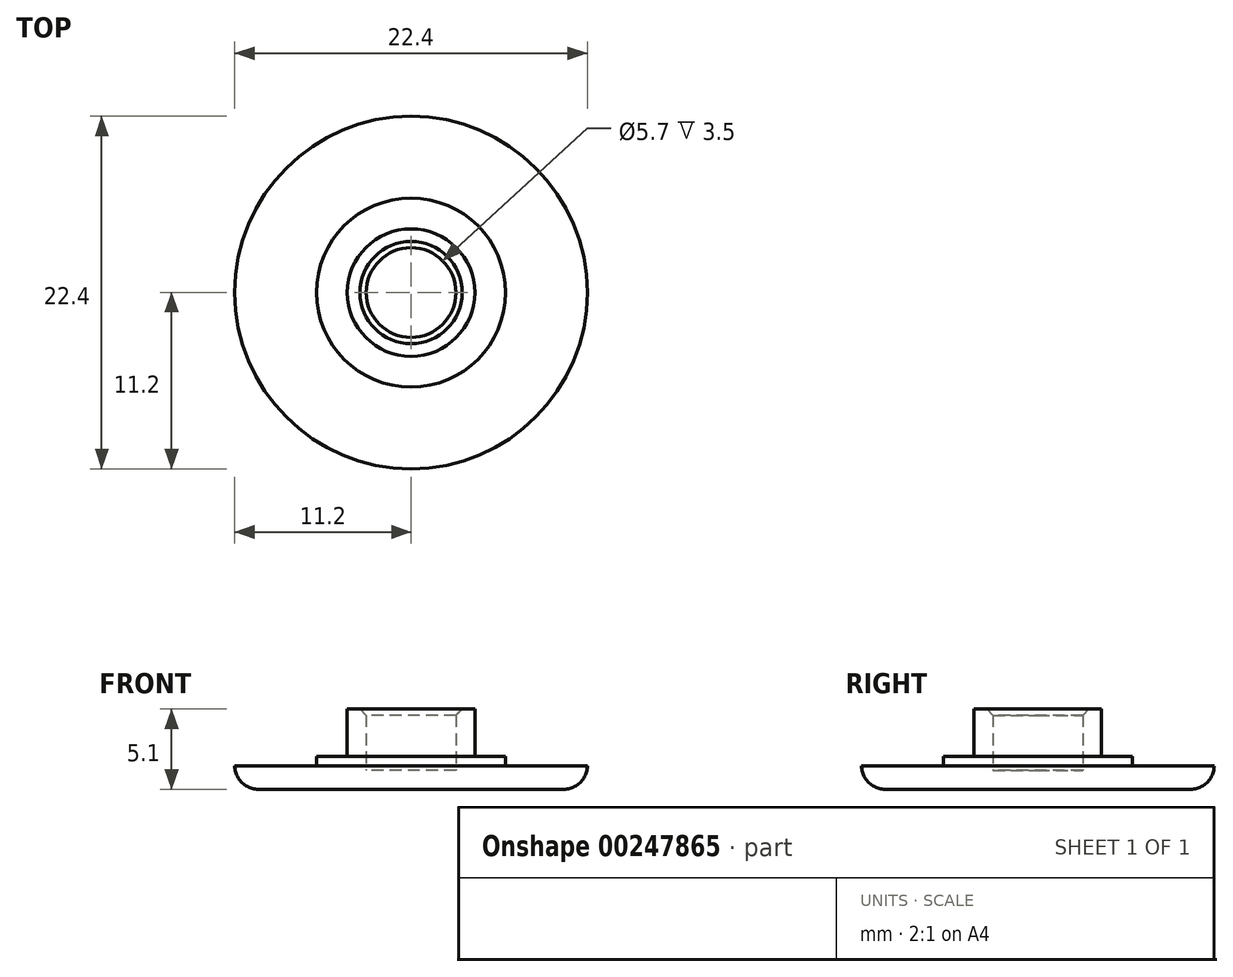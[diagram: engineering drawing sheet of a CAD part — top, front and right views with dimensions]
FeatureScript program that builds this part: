
annotation { "Feature Type Name" : "Feature", "Feature Type Description" : "" }
export const myFeature = defineFeature(function(context is Context, id is Id, definition is map)
    precondition{}
    {
        {
            var Q0;
            Q0=qCreatedBy(makeId("Top.planeOp"),FACE);
            var sketch = newSketch(context, id + "F0", { "sketchPlane" : qUnion([Q0])});
            skCircle(sketch, "E0", {"center": v(0, 0) * mm, "radius": 11.2 * mm});
            skSolve(sketch);
        }
        {
            var Q0;
            Q0=makeQuery(id+"F0.imprint","IMPRINT",FACE,{"disambiguationData":[TD([[makeQuery(id+"F0.imprint","IMPRINT",EDGE,{"derivedFrom":sQuery(id+"F0.wireOp",EDGE,"E0")}),1.0]])]});
            extrude(context, id + "F1", {"entities" : qUnion([Q0]), "oppositeDirection" : true, "depth" : 1.5 * mm, "offsetDistance" : 25 * mm});
        }
        {
            var Q0;
            Q0=makeQuery(id+"F1.opExtrude","CAP_FACE",FACE,{"disambiguationData":[OSD([sQuery(id+"F0.wireOp",EDGE,"E0")])],"isStart":true});
            var sketch = newSketch(context, id + "F2", { "sketchPlane" : qUnion([Q0])});
            skCircle(sketch, "E1", {"center": v(0, 0) * mm, "radius": 6 * mm});
            skSolve(sketch);
        }
        {
            var Q0;
            Q0 = qSketchRegion(id + "F2", true);
            extrude(context, id + "F3", {"entities" : qUnion([Q0]), "operationType" : NewBodyOperationType.ADD, "depth" : 0.6 * mm, "offsetDistance" : 25 * mm});
        }
        {
            var Q0;
            Q0=makeQuery(id+"F3.opExtrude","CAP_FACE",FACE,{"disambiguationData":[OSD([sQuery(id+"F2.wireOp",EDGE,"E1")])],"isStart":false});
            var sketch = newSketch(context, id + "F4", { "sketchPlane" : qUnion([Q0])});
            skCircle(sketch, "E2", {"center": v(0, 0) * mm, "radius": 4.05 * mm});
            skSolve(sketch);
        }
        {
            var Q0;
            Q0 = qSketchRegion(id + "F4", true);
            extrude(context, id + "F5", {"entities" : qUnion([Q0]), "operationType" : NewBodyOperationType.ADD, "depth" : 3 * mm, "offsetDistance" : 25 * mm});
        }
        {
            var Q0;
            Q0=makeQuery(id+"F5.opExtrude","CAP_FACE",FACE,{"disambiguationData":[OSD([sQuery(id+"F4.wireOp",EDGE,"E2")])],"isStart":false});
            shell(context, id + "F6", {"entities" : qUnion([Q0]), "thickness" : 1.2 * mm});
        }
        {
            var Q0;
            Q0=makeQuery(id+"F1.opExtrude","CAP_EDGE",EDGE,{"disambiguationData":[OSD([sQuery(id+"F0.wireOp",EDGE,"E0")])],"isStart":false});
            fillet(context, id + "F7", {"entities" : qUnion([Q0]), "radius" : 1.5 * mm, "tangentPropagation" : true, "allowEdgeOverflow" : false});
        }
        {
            var Q0;
            Q0=makeQuery(id+"F6.opShell","OFFSET_EDGE",EDGE,{"disambiguationData":[OSD([sQuery(id+"F4.wireOp",EDGE,"E2")])]});
            chamfer(context, id + "F8", {"entities" : qUnion([Q0]), "width" : 0.4 * mm, "tangentPropagation" : true});
        }
    });
